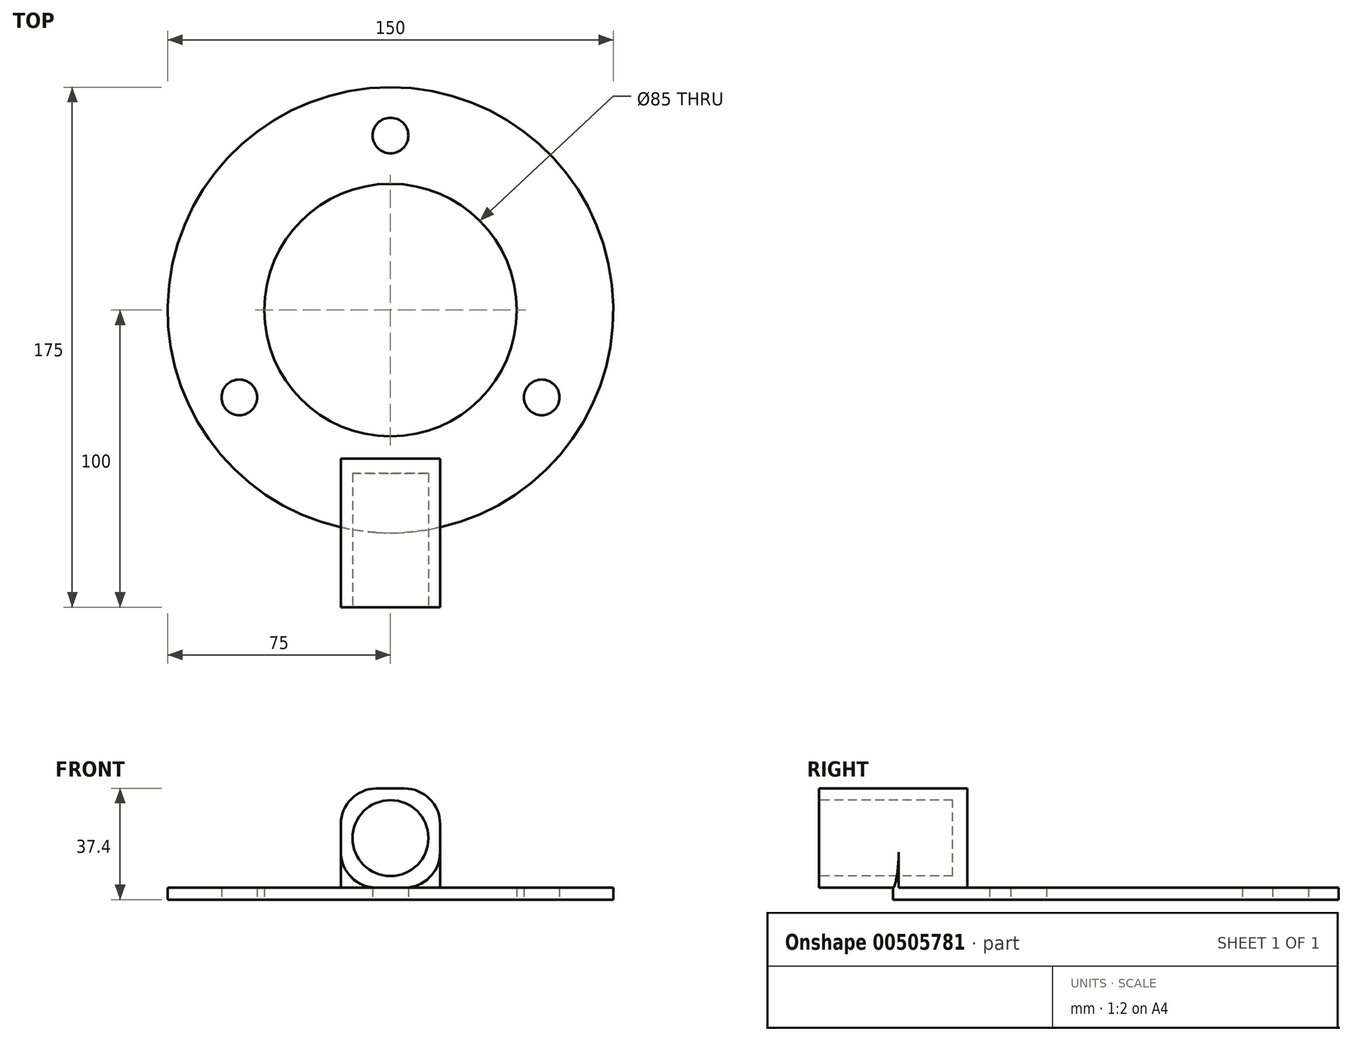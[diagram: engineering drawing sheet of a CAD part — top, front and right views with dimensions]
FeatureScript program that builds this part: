
annotation { "Feature Type Name" : "Feature", "Feature Type Description" : "" }
export const myFeature = defineFeature(function(context is Context, id is Id, definition is map)
    precondition{}
    {
        {
            var Q0;
            Q0=qCreatedBy(makeId("Top.planeOp"),FACE);
            var sketch = newSketch(context, id + "F0", { "sketchPlane" : qUnion([Q0])});
            skCircle(sketch, "E0", {"center": v(0, 0) * mm, "radius": 75 * mm});
            skCircle(sketch, "E1", {"center": v(0, 0) * mm, "radius": 42.5 * mm});
            skLineSegment(sketch, "E2", {"start": v(0, 0) * mm, "end": v(0, 153.74) * mm, "construction": true});
            skLineSegment(sketch, "E3", {"start": v(0, 0) * mm, "end": v(135.12, -78.01) * mm, "construction": true});
            skLineSegment(sketch, "E4", {"start": v(0, 0) * mm, "end": v(-147.86, -85.37) * mm, "construction": true});
            skCircle(sketch, "E5", {"center": v(50.88, -29.37) * mm, "radius": 6 * mm});
            skCircle(sketch, "E6", {"center": v(0, 0) * mm, "radius": 58.75 * mm, "construction": true});
            skCircle(sketch, "E7.1.0", {"center": v(0, 58.75) * mm, "radius": 6 * mm});
            skCircle(sketch, "E7.2.0", {"center": v(-50.88, -29.37) * mm, "radius": 6 * mm});
            skSolve(sketch);
        }
        {
            var Q0;
            Q0 = qSketchRegion(id + "F0", true);
            extrude(context, id + "F1", {"entities" : qUnion([Q0]), "depth" : 4 * mm});
        }
        {
            var Q0;
            Q0=makeQuery(id+"F1.opExtrude","CAP_FACE",FACE,{"disambiguationData":[OSD([sQuery(id+"F0.wireOp",EDGE,"E0"),sQuery(id+"F0.wireOp",EDGE,"E1"),sQuery(id+"F0.wireOp",EDGE,"E5"),sQuery(id+"F0.wireOp",EDGE,"E7.1.0"),sQuery(id+"F0.wireOp",EDGE,"E7.2.0")])],"isStart":false});
            var sketch = newSketch(context, id + "F2", { "sketchPlane" : qUnion([Q0])});
            skLineSegment(sketch, "E8", {"start": v(0, 0) * mm, "end": v(0, -205.23) * mm, "construction": true});
            skLineSegment(sketch, "E9.bottom", {"start": v(16.7, -100) * mm, "end": v(-16.7, -100) * mm});
            skLineSegment(sketch, "E9.top", {"start": v(16.7, -50) * mm, "end": v(-16.7, -50) * mm});
            skLineSegment(sketch, "E9.left", {"start": v(16.7, -100) * mm, "end": v(16.7, -50) * mm});
            skLineSegment(sketch, "E9.right", {"start": v(-16.7, -100) * mm, "end": v(-16.7, -50) * mm});
            skPoint(sketch, "E9.middle", {"position": v(0, -75) * mm});
            skSolve(sketch);
        }
        {
            var Q0;
            Q0 = qSketchRegion(id + "F2", true);
            extrude(context, id + "F3", {"entities" : qUnion([Q0]), "operationType" : NewBodyOperationType.ADD, "depth" : 33.4 * mm});
        }
        {
            var Q0;
            Q0=makeQuery(id+"F3.opExtrude","CAP_EDGE",EDGE,{"disambiguationData":[OSD([sQuery(id+"F2.wireOp",EDGE,"E9.left")])],"isStart":false});
            var Q1;
            Q1=makeQuery(id+"F3.opExtrude","CAP_EDGE",EDGE,{"disambiguationData":[OSD([sQuery(id+"F2.wireOp",EDGE,"E9.right")])],"isStart":false});
            fillet(context, id + "F4", {"entities" : qUnion([Q0, Q1]), "radius" : 12 * mm, "tangentPropagation" : true, "allowEdgeOverflow" : false});
        }
        {
            var Q0;
            Q0=makeQuery(id+"F3.opExtrude","SWEPT_FACE",FACE,{"disambiguationData":[OSD([sQuery(id+"F2.wireOp",EDGE,"E9.bottom")])]});
            var sketch = newSketch(context, id + "F5", { "sketchPlane" : qUnion([Q0])});
            skLineSegment(sketch, "E10", {"start": v(0, 37.4) * mm, "end": v(0, 4) * mm, "construction": true});
            skCircle(sketch, "E11", {"center": v(0, 20.7) * mm, "radius": 12.78 * mm});
            skSolve(sketch);
        }
        {
            var Q0;
            Q0 = qSketchRegion(id + "F5", true);
            extrude(context, id + "F6", {"entities" : qUnion([Q0]), "operationType" : NewBodyOperationType.REMOVE, "oppositeDirection" : true, "depth" : 45 * mm});
        }
        {
            var Q0;
            {var subQ0=sQuery(id+"F2.wireOp",EDGE,"E9.left");Q0=makeQuery(id+"F3.boolean.opBoolean","SPLIT",EDGE,{"disambiguationData":[topologyDisambiguationEdgeConnected([makeQuery(id+"F1.opExtrude","CAP_FACE",FACE,{"disambiguationData":[OSD([sQuery(id+"F0.wireOp",EDGE,"E0"),sQuery(id+"F0.wireOp",EDGE,"E1"),sQuery(id+"F0.wireOp",EDGE,"E5"),sQuery(id+"F0.wireOp",EDGE,"E7.1.0"),sQuery(id+"F0.wireOp",EDGE,"E7.2.0")])],"isStart":false})])],"derivedFrom":makeQuery(id+"F3.opExtrude","CAP_EDGE",EDGE,{"disambiguationData":[OSD([subQ0])],"isStart":true})});}
            var Q1;
            {var subQ0=sQuery(id+"F2.wireOp",EDGE,"E9.right");Q1=makeQuery(id+"F3.boolean.opBoolean","SPLIT",EDGE,{"disambiguationData":[topologyDisambiguationEdgeConnected([makeQuery(id+"F1.opExtrude","CAP_FACE",FACE,{"disambiguationData":[OSD([sQuery(id+"F0.wireOp",EDGE,"E0"),sQuery(id+"F0.wireOp",EDGE,"E1"),sQuery(id+"F0.wireOp",EDGE,"E5"),sQuery(id+"F0.wireOp",EDGE,"E7.1.0"),sQuery(id+"F0.wireOp",EDGE,"E7.2.0")])],"isStart":false})])],"derivedFrom":makeQuery(id+"F3.opExtrude","CAP_EDGE",EDGE,{"disambiguationData":[OSD([subQ0])],"isStart":true})});}
            fillet(context, id + "F7", {"entities" : qUnion([Q0, Q1]), "radius" : 12 * mm, "tangentPropagation" : true, "allowEdgeOverflow" : false});
        }
    });
